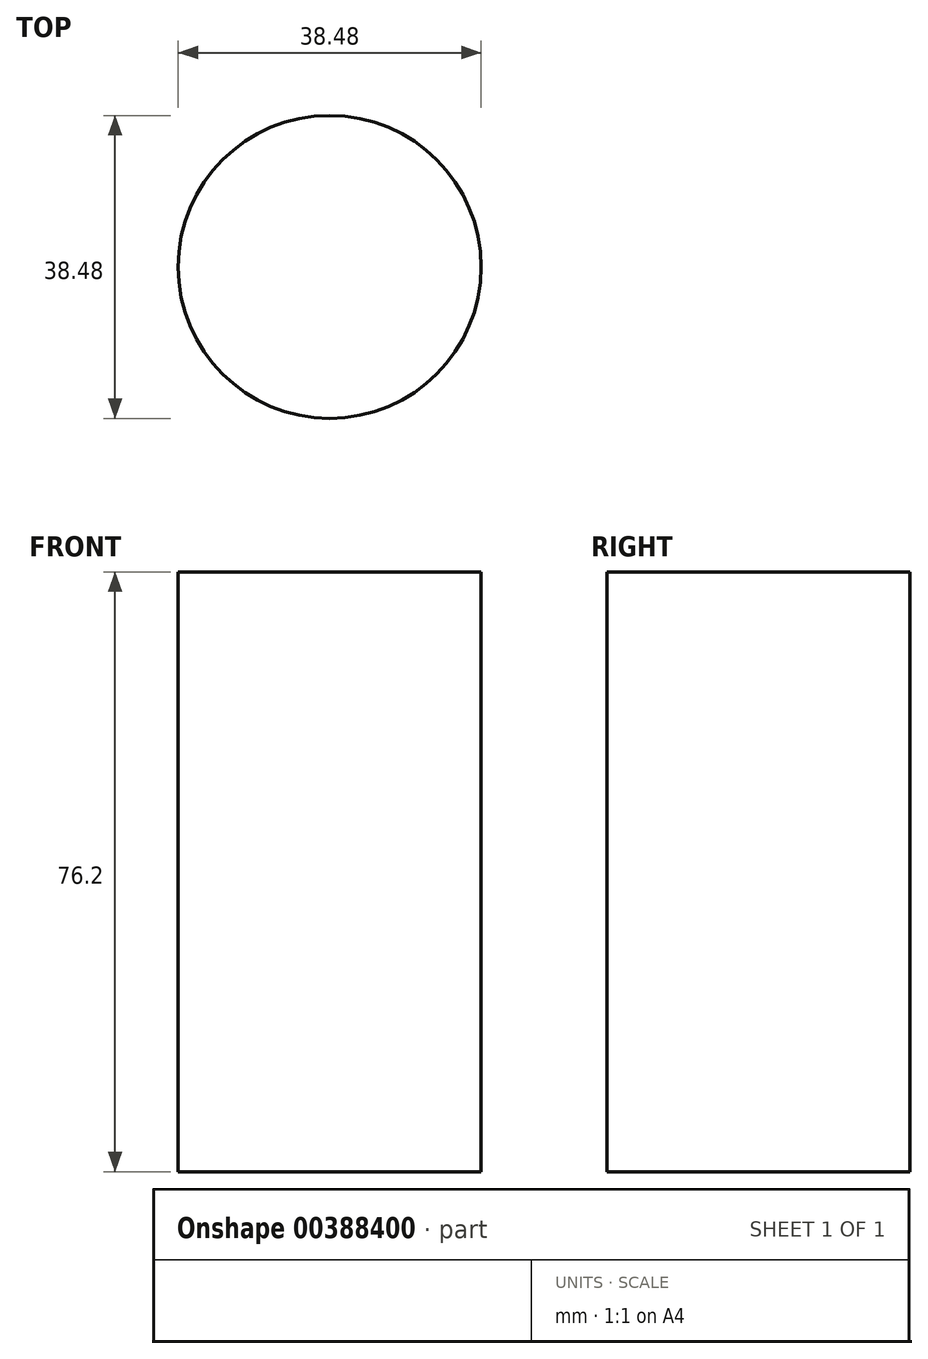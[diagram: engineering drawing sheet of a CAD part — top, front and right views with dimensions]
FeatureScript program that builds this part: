
annotation { "Feature Type Name" : "Feature", "Feature Type Description" : "" }
export const myFeature = defineFeature(function(context is Context, id is Id, definition is map)
    precondition{}
    {
        {
            var Q0;
            Q0=qCreatedBy(makeId("Top.planeOp"),FACE);
            var sketch = newSketch(context, id + "F0", { "sketchPlane" : qUnion([Q0])});
            skCircle(sketch, "E0", {"center": v(0, 0) * mm, "radius": 19.24 * mm});
            skSolve(sketch);
        }
        {
            var Q0;
            Q0=sQuery(id+"F0.wireOp",EDGE,"E0");
            extrude(context, id + "F1", {"bodyType" : ToolBodyType.SURFACE, "surfaceEntities" : qUnion([Q0]), "depth" : 76.2 * mm});
        }
    });
